# Revit family: ElectricalFixture_WiringAccessories_Hager_Sollysta_DecorativeFlatEuroPlates
name_source: partatom
category: Electrical Fixtures
revit_build: Autodesk Revit 2015 (Build: 20160512_1515(x64)
units: mm (PartAtom-declared; Revit-internal decimal feet)

## types (18) — shared parameters
CE Approval = Yes
Default Elevation = 1219.2 mm  [stored 4 ft]
Design Country = China
Expected Life = 25 years
Extrusion From Wall = 3 mm  [stored 0.00984252 ft]
Frequency = 50/60Hz
Gross Weight kg = 0.165
LED Indicator Switch = No
Manufacturer = Hager
Manufacturer Country = United Kingdom
Manufacturer Website = http://www.hager.co.uk
Overall Depth = 26.1 mm
Overall Height = 86 mm  [stored 0.282152 ft]
Packaging Recyclable = Yes
Product Family = DecorativeEuroAccomodationPlates&Modules
Product Group = WiringAccessories
Product Literature = http://www.hager.co.uk
Product Range = Sollysta
Product URL = http://www.hager.co.uk
Reference Standard = BS 1363-2
Shape = Rectangular
Shipping Weight kg = 0.188
Supply Phase = 1
Switch = Yes
Switch Width = 100 mm  [stored 0.328084 ft]
SwitchHeight = 50 mm  [stored 0.164042 ft]
Type = ElectricalFixture
Voltage (Volts) = 230V/240V

## per-type parameters (varying)
| type | 1Gang | 2Gang | 4Gang | Colour | Description | EAN Code | Features | Finish | Material | Name | Overall Length | Overall Width | Product Model Number | Technical Description | Unique Reference |
| WFP1EUPSW | Yes | No | No | PolishedSteel | EuroStylePlate1ModulePolishedSteelWhiteInsert | 5015654742942 | EuroStylePlate1ModulePolishedSteelWhiteInsert | Polished | Hager_PolishedSteel | DecorativeEuroAccomodationPlates&Modules_WFP1EUPSW | 86 mm  [stored 0.282152 ft] | 86 mm  [stored 0.282152 ft] | WRP1EUPSW | EuroStylePlate1ModulePolishedSteelWhiteInsert | WRP1EUPSW |
| WFP1EUBSW | Yes | No | No | BrushedSteel | EuroStylePlate1ModuleBrushedSteelWhiteInsert | 5015654742980 | EuroStylePlate1ModuleBrushedSteelWhiteInsert | Brushed | Hager_BrushedSteel | DecorativeEuroAccomodationPlates&Modules_WFP1EUBSW | 86 mm  [stored 0.282152 ft] | 86 mm  [stored 0.282152 ft] | WFP1EUBSW | EuroStylePlate1ModuleBrushedSteelWhiteInsert | WFP1EUBSW |
| WFP1EUPBW | Yes | No | No | PolishedBrass | EuroStylePlate1ModulePolishedBrassWhiteInsert | 5015654743024 | EuroStylePlate1ModulePolishedBrassWhiteInsert | Polished | Hager_PolishedBrass | DecorativeEuroAccomodationPlates&Modules_WFP1EUPBW | 86 mm  [stored 0.282152 ft] | 86 mm  [stored 0.282152 ft] | WFP1EUPBW | EuroStylePlate1ModulePolishedBrassWhiteInsert | WFP1EUPBW |
| WFP1EUBNB | Yes | No | No | BlackNickel | EuroStylePlate1ModuleBlackNickelBlackInsert | 5015654743062 | EuroStylePlate1ModuleBlackNickelBlackInsert | Polished | Hager_BlackNickel | DecorativeEuroAccomodationPlates&Modules_WFP1EUBNB | 86 mm  [stored 0.282152 ft] | 86 mm  [stored 0.282152 ft] | WFP1EUBNB | EuroStylePlate1ModuleBlackNickelBlackInsert | WFP1EUBNB |
| WFP1EUPSB | Yes | No | No | PolishedSteel | EuroStylePlate1ModulePolishedSteelBlackInsert | 5015654742966 | EuroStylePlate1ModulePolishedSteelBlackInsert | Polished | Hager_PolishedSteel | DecorativeEuroAccomodationPlates&Modules_WFP1EUPSB | 86 mm  [stored 0.282152 ft] | 86 mm  [stored 0.282152 ft] | WFP1EUPSB | EuroStylePlate1ModulePolishedSteelBlackInsert | WFP1EUPSB |
| WFP1EUBSB | Yes | No | No | BrushedSteel | EuroStylePlate1ModuleBrushedSteelBlackInsert | 5015654743000 | EuroStylePlate1ModuleBrushedSteelBlackInsert | Brushed | Hager_BrushedSteel | DecorativeEuroAccomodationPlates&Modules_WFP1EUBSB | 86 mm  [stored 0.282152 ft] | 86 mm  [stored 0.282152 ft] | WFP1EUBSB | EuroStylePlate1ModuleBrushedSteelBlackInsert | WFP1EUBSB |
| WFP1EUPBB | Yes | No | No | PolishedBrass | EuroStylePlate1ModulePolishedBrassBlackInsert | 5015654743048 | EuroStylePlate1ModulePolishedBrassBlackInsert | Polished | Hager_PolishedBrass | DecorativeEuroAccomodationPlates&Modules_WFP1EUPBB | 86 mm  [stored 0.282152 ft] | 86 mm  [stored 0.282152 ft] | WFP1EUPBB | EuroStylePlate1ModulePolishedBrassBlackInsert | WFP1EUPBB |
| WFP2EUPSW | No | Yes | No | PolishedSteel | EuroStylePlate2ModulePolishedSteelWhiteInsert | 5015654743086 | EuroStylePlate2ModulePolishedSteelWhiteInsert | Polished | Hager_PolishedSteel | DecorativeEuroAccomodationPlates&Modules_WFP2EUPSW | 86 mm  [stored 0.282152 ft] | 86 mm  [stored 0.282152 ft] | WFP2EUPSW | EuroStylePlate2ModulePolishedSteelWhiteInsert | WFP2EUPSW |
| WFP2EUPBW | No | Yes | No | PolishedBrass | EuroStylePlate2ModulePolishedBrassWhiteInsert | 5015654743161 | EuroStylePlate2ModulePolishedBrassWhiteInsert | Polished | Hager_PolishedBrass | DecorativeEuroAccomodationPlates&Modules_WFP2EUPBW | 86 mm  [stored 0.282152 ft] | 86 mm  [stored 0.282152 ft] | WFP2EUPBW | EuroStylePlate2ModulePolishedBrassWhiteInsert | WFP2EUPBW |
| WFP2EUPSB | No | Yes | No | PolishedSteel | EuroStylePlate2ModulePolishedSteelBlackInsert | 5015654743109 | EuroStylePlate2ModulePolishedSteelBlackInsert | Polished | Hager_PolishedSteel | DecorativeEuroAccomodationPlates&Modules_WFP2EUPSB | 86 mm  [stored 0.282152 ft] | 86 mm  [stored 0.282152 ft] | WFP2EUPSB | EuroStylePlate2ModulePolishedSteelBlackInsert | WFP2EUPSB |
| WFP2EUPBB | No | Yes | No | PolishedBrass | EuroStylePlate2ModulePolishedBrassBlackInsert | 5015654743185 | EuroStylePlate2ModulePolishedBrassBlackInsert | Polished | Hager_PolishedBrass | DecorativeEuroAccomodationPlates&Modules_WFP2EUPBB | 86 mm  [stored 0.282152 ft] | 86 mm  [stored 0.282152 ft] | WFP2EUPBB | EuroStylePlate2ModulePolishedBrassBlackInsert | WFP2EUPBB |
| WFP4EUPSW | No | Yes | Yes | PolishedSteel | EuroStylePlate4ModulePolishedSteelWhiteInsert | 5015654743222 | EuroStylePlate4ModulePolishedSteelWhiteInsert | Polished | Hager_PolishedSteel | DecorativeEuroAccomodationPlates&Modules_WFP4EUPSW | 146 mm  [stored 0.479003 ft] | 146 mm  [stored 0.479003 ft] | WFP4EUPSW | EuroStylePlate4ModulePolishedSteelWhiteInsert | WFP4EUPSW |
| WFP4EUBSW | No | Yes | Yes | BrushedSteel | EuroStylePlate4ModuleBrushedSteelWhiteInsert | 5015654743260 | EuroStylePlate4ModuleBrushedSteelWhiteInsert | Brushed | Hager_BrushedSteel | DecorativeEuroAccomodationPlates&Modules_WFP4EUBSW | 146 mm  [stored 0.479003 ft] | 146 mm  [stored 0.479003 ft] | WFP4EUBSW | EuroStylePlate4ModuleBrushedSteelWhiteInsert | WFP4EUBSW |
| WFP4EUPBW | No | Yes | Yes | PolishedBrass | EuroStylePlate4ModulePolishedBrassWhiteInsert | 5015654743307 | EuroStylePlate4ModulePolishedBrassWhiteInsert | Polished | Hager_PolishedBrass | DecorativeEuroAccomodationPlates&Modules_WFP4EUPBW | 146 mm  [stored 0.479003 ft] | 146 mm  [stored 0.479003 ft] | WFP4EUPBW | EuroStylePlate4ModulePolishedBrassWhiteInsert | WFP4EUPBW |
| WFP4EUPSB | No | Yes | Yes | PolishedSteel | EuroStylePlate4ModulePolishedSteelBlackInsert | 5015654743239 | EuroStylePlate4ModulePolishedSteelBlackInsert | Polished | Hager_PolishedSteel | DecorativeEuroAccomodationPlates&Modules_WFP4EUPSB | 146 mm  [stored 0.479003 ft] | 146 mm  [stored 0.479003 ft] | 5015654743246 | EuroStylePlate4ModulePolishedSteelBlackInsert | 5015654743246 |
| WFP4EUBSB | No | Yes | Yes | BrushedSteel | EuroStylePlate4ModuleBrushedSteelBlackInsert | 5015654743284 | EuroStylePlate4ModuleBrushedSteelBlackInsert | Brushed | Hager_BrushedSteel | DecorativeEuroAccomodationPlates&Modules_WFP4EUBSB | 146 mm  [stored 0.479003 ft] | 146 mm  [stored 0.479003 ft] | WFP4EUBSB | EuroStylePlate4ModuleBrushedSteelBlackInsert | WFP4EUBSB |
| WFP4EUPBB | No | Yes | Yes | PolishedBrass | EuroStylePlate4ModulePolishedBrassBlackInsert | 5015654743314 | EuroStylePlate4ModulePolishedBrassBlackInsert | Polished | Hager_PolishedBrass | DecorativeEuroAccomodationPlates&Modules_WFP4EUPBB | 146 mm  [stored 0.479003 ft] | 146 mm  [stored 0.479003 ft] | 5015654743321 | EuroStylePlate4ModulePolishedBrassBlackInsert | 5015654743321 |
| WFP4EUBNB | No | Yes | Yes | BlackNickel | EuroStylePlate4ModuleBlackNickelBlackInsert | 5015654743345 | EuroStylePlate4ModuleBlackNickelBlackInsert | Polished | Hager_BlackNickel | DecorativeEuroAccomodationPlates&Modules_WFP4EUBNB | 146 mm  [stored 0.479003 ft] | 146 mm  [stored 0.479003 ft] | WFP4EUBNB | EuroStylePlate4ModuleBlackNickelBlackInsert | WFP4EUBNB |

note: [stored X ft] marks values corroborated as IEEE doubles in the binary element streams (Revit-internal decimal feet)

## geometry (parser evidence)
native form markers: Blend x4, Sweep x24
no freeform markers — native parametric forms only
